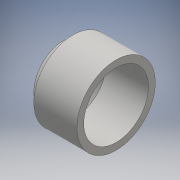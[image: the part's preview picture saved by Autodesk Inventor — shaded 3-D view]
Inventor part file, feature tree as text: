
AUTODESK INVENTOR PART (.ipt)
format: ipt  version: 2016 (Build 200138000, 138)  size: 121,856 bytes
history: native  units: mm
features: chamfer x2, revolve x1, fillet x1, sketch x1
ambient origin geometry x8: Origin, YZ Plane, XZ Plane, XY Plane, X Axis, Y Axis, Z Axis, Center Point
bodies: Solid1 (feature_tree)
feature tree (5):
  revolve  "Revolution1"  [1 undecoded]
  chamfer  "Chamfer1"  Distance=20.0mm
  chamfer  "Chamfer2"  Distance=3.0mm
  fillet  "Fillet1"  Radius=3.0mm
  sketch  "Sketch1"  dims[d0=0.349066mm d1=28.5mm d2=20.0mm d3=3.0mm d4=3.0mm d5=90.0deg d6=7.0mm d7=2.0mm d8=4.0mm d9=2.0mm d10=45.0deg d11=2.0mm d12=2.0mm d13=45.0deg d14=27.103169mm]
note: 1 required parameter value undecoded (feature->parameter linkage not recoverable at this tier; creation-order binding heuristic only, values carry confidence <= 0.55)
